# Revit family: Storage-Freestanding-Teknion-JNFPS-Pedestal-R2015
name_source: partatom
category: Furniture
revit_build: Autodesk Revit Architecture 2015 (Build: 20140323_1530(x64)
units: mm (PartAtom-declared; Revit-internal decimal feet)

## types (2) — shared parameters
Assembly Code = E2020200
Height = 27.48 "
Lock Depth = -0.1 "
Manufacturer = Teknion
Manufacturer Fax = 416.661.4586
Part Number = JNFPS
Product Documentation Link = http://www.teknion.com
Product Line = expansion cityline
Product Page URL = http://www.teknion.com
Series = expansion cityline
Sustainability Data = http://www.teknion.com
URL = www.teknion.com
Unit Weight URL = http://www.teknion.com
Warranty = http://www.teknion.com
Width = 16.13 "

## per-type parameters (varying)
| type | Description | Front Case Thickness | Front Finish | Model |
| Metal | Pedestal - Metal Front Case -W16" x H24" | 0.118 " | Mica - Teknion - V - Satin - Very White | JNFPSM__1624_ |
| Solid | Pedestal - Solid Front Case -W16" x H24" | 0.701 " | Source Laminate - Teknion - XS - Storm White | JNFPSS__1624_ |

## geometry (parser evidence)
native form markers: Sweep x2
no freeform markers — native parametric forms only
